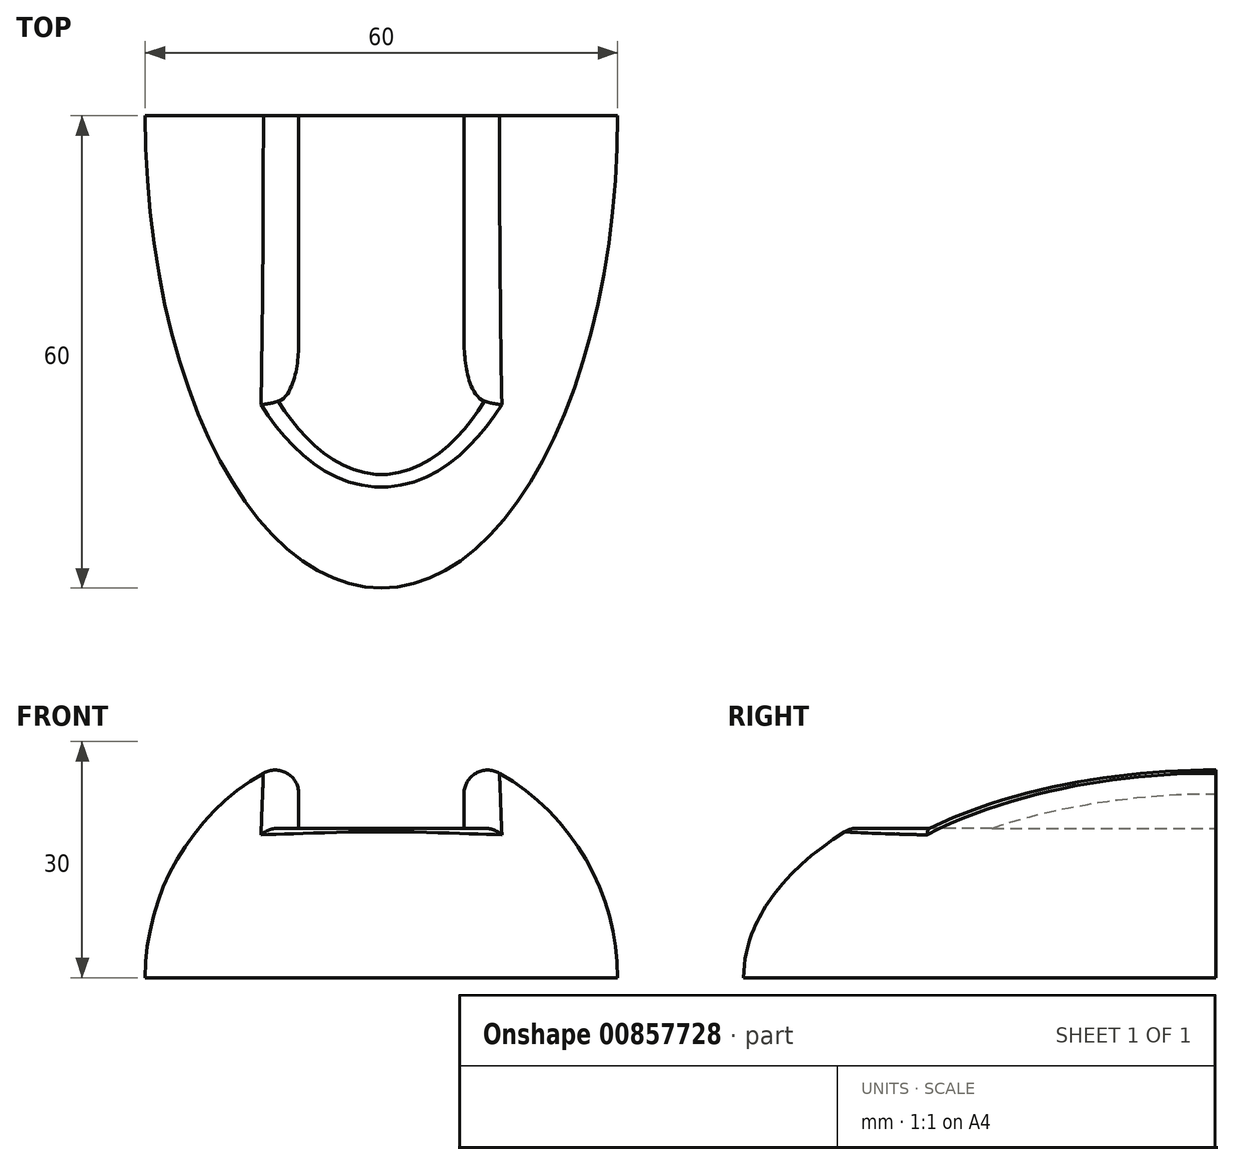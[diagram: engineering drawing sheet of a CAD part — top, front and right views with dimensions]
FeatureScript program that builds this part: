
annotation { "Feature Type Name" : "Feature", "Feature Type Description" : "" }
export const myFeature = defineFeature(function(context is Context, id is Id, definition is map)
    precondition{}
    {
        {
            var Q0;
            Q0=qCreatedBy(makeId("Right.planeOp"),FACE);
            var sketch = newSketch(context, id + "F0", { "sketchPlane" : qUnion([Q0])});
            skEllipticalArc(sketch, "E0", {});
            skLineSegment(sketch, "E1", {"start": v(-60, 0) * mm, "end": v(60, 0) * mm});
            const initialGuessF0  = {"E0": [0, 0, 0, 1, 0.03, 0.06, 4.71238898038469, 1.5707963267948966]};
            skSetInitialGuess(sketch, initialGuessF0);
            skSolve(sketch);
        }
        {
            var Q0;
            Q0=qSketchRegion(id+"F0",true);
            var Q1;
            Q1=sQuery(id+"F0.wireOp",EDGE,"E1");
            revolve(context, id + "F1", {"surfaceOperationType" : NewSurfaceOperationType.NEW, "entities" : qUnion([Q0]), "axis" : qUnion([Q1]), "revolveType" : RevolveType.SYMMETRIC, "angle" : 180 * degree});
        }
        {
            var Q0;
            Q0=qCreatedBy(makeId("Top.planeOp"),FACE);
            cPlane(context, id + "F2", {"entities" : qUnion([Q0]), "cplaneType" : CPlaneType.OFFSET, "offset" : 19 * mm, "width" : 150 * mm, "height" : 150 * mm});
        }
        {
            var Q0;
            Q0=qCreatedBy(id+"F2.planeOp",FACE);
            var sketch = newSketch(context, id + "F3", { "sketchPlane" : qUnion([Q0])});
            skLineSegment(sketch, "E2.bottom", {"start": v(10.5, -100) * mm, "end": v(-10.5, -100) * mm});
            skLineSegment(sketch, "E2.top", {"start": v(10.5, 100) * mm, "end": v(-10.5, 100) * mm});
            skLineSegment(sketch, "E2.left", {"start": v(10.5, -100) * mm, "end": v(10.5, 100) * mm});
            skLineSegment(sketch, "E2.right", {"start": v(-10.5, -100) * mm, "end": v(-10.5, 100) * mm});
            skPoint(sketch, "E2.middle", {"position": v(0, 0) * mm});
            skSolve(sketch);
        }
        {
            var Q0;
            Q0=qSketchRegion(id+"F3",true);
            extrude(context, id + "F4", {"entities" : qUnion([Q0]), "operationType" : NewBodyOperationType.REMOVE, "endBound" : BoundingType.THROUGH_ALL, "depth" : 25 * mm, "offsetDistance" : 25 * mm});
        }
        {
            var Q0;
            Q0=qCreatedBy(makeId("Top.planeOp"),FACE);
            var sketch = newSketch(context, id + "F5", { "sketchPlane" : qUnion([Q0])});
            skLineSegment(sketch, "E3.bottom", {"start": v(-193.83, 0) * mm, "end": v(210.63, 0) * mm});
            skLineSegment(sketch, "E3.top", {"start": v(-193.83, 200) * mm, "end": v(210.63, 200) * mm});
            skLineSegment(sketch, "E3.left", {"start": v(-193.83, 0) * mm, "end": v(-193.83, 200) * mm});
            skLineSegment(sketch, "E3.right", {"start": v(210.63, 0) * mm, "end": v(210.63, 200) * mm});
            skSolve(sketch);
        }
        {
            var Q0;
            Q0=qSketchRegion(id+"F5",true);
            extrude(context, id + "F6", {"entities" : qUnion([Q0]), "operationType" : NewBodyOperationType.REMOVE, "endBound" : BoundingType.THROUGH_ALL, "depth" : 25 * mm, "offsetDistance" : 25 * mm});
        }
        {
            var Q0;
            Q0=makeQuery(id+"F4.boolean.opBoolean","INTERSECT",EDGE,{"derivedFrom":[makeQuery(id+"F1.opRevolve","SWEPT_FACE",FACE,{"disambiguationData":[OSD([sQuery(id+"F0.wireOp",EDGE,"E0")])]}),makeQuery(id+"F4.opExtrude","SWEPT_FACE",FACE,{"disambiguationData":[OSD([sQuery(id+"F3.wireOp",EDGE,"E2.right")])]})]});
            var Q1;
            Q1=makeQuery(id+"F4.boolean.opBoolean","INTERSECT",EDGE,{"derivedFrom":[makeQuery(id+"F1.opRevolve","SWEPT_FACE",FACE,{"disambiguationData":[OSD([sQuery(id+"F0.wireOp",EDGE,"E0")])]}),makeQuery(id+"F4.opExtrude","SWEPT_FACE",FACE,{"disambiguationData":[OSD([sQuery(id+"F3.wireOp",EDGE,"E2.left")])]})]});
            var Q2;
            Q2=makeQuery(id+"F4.boolean.opBoolean","INTERSECT",EDGE,{"disambiguationData":[OD(0.0)],"derivedFrom":[makeQuery(id+"F1.opRevolve","SWEPT_FACE",FACE,{"disambiguationData":[OSD([sQuery(id+"F0.wireOp",EDGE,"E0")])]}),makeQuery(id+"F4.opExtrude","CAP_FACE",FACE,{"disambiguationData":[OSD([sQuery(id+"F3.wireOp",EDGE,"E2.bottom"),sQuery(id+"F3.wireOp",EDGE,"E2.top"),sQuery(id+"F3.wireOp",EDGE,"E2.left"),sQuery(id+"F3.wireOp",EDGE,"E2.right")])],"isStart":true})]});
            fillet(context, id + "F7", {"entities" : qUnion([Q0, Q1, Q2]), "radius" : 3 * mm, "tangentPropagation" : true, "allowEdgeOverflow" : false});
        }
    });
